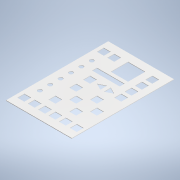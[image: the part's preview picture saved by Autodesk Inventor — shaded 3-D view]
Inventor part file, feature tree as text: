
AUTODESK INVENTOR PART (.ipt)
format: ipt  version: 2021.1 (Build 251245000, 245)  size: 239,616 bytes
history: native  units: mm
features: extrude x3, sketch x3
ambient origin geometry x8: Origin, YZ Plane, XZ Plane, XY Plane, X Axis, Y Axis, Z Axis, Center Point
bodies: Solid1 (feature_tree)
feature tree (6):
  extrude  "Extrusion1"  Depth=1.5875mm TaperAngle=0.0deg
  extrude  "Extrusion2"  [1 undecoded]
  extrude  "Extrusion3"  [1 undecoded]
  sketch  "Sketch1"  dims[d4=1.5875mm d5=0.0mm d6=12.7mm d7=0.0mm]
  sketch  "Sketch2"  dims[d8=12.7mm d9=0.0mm]
  sketch  "Sketch3"
note: 2 required parameter values undecoded (feature->parameter linkage not recoverable at this tier; creation-order binding heuristic only, values carry confidence <= 0.55)
